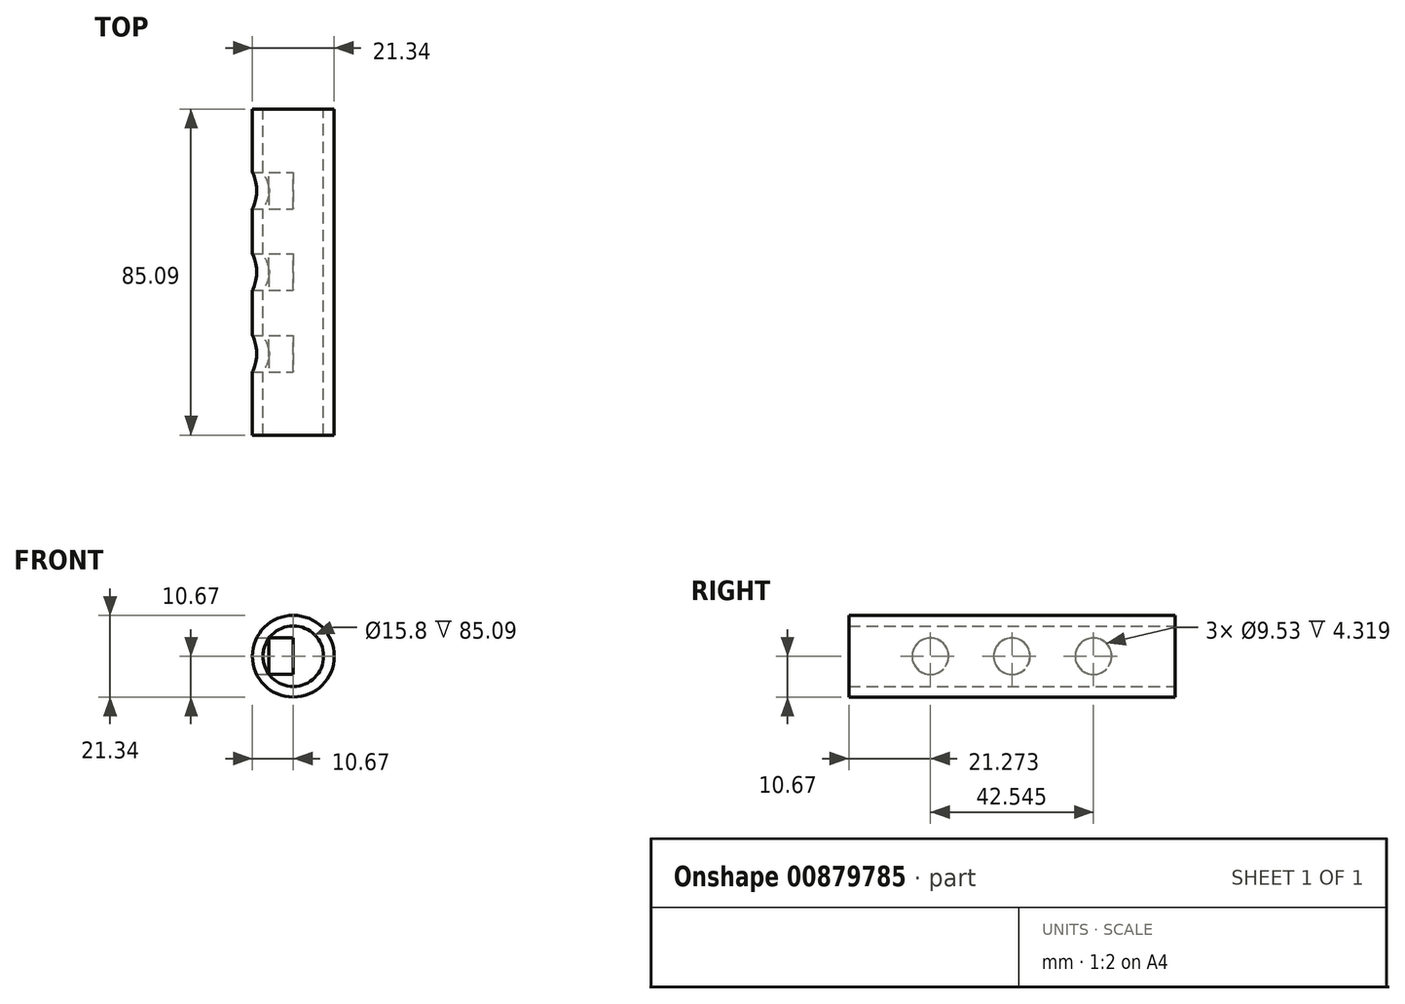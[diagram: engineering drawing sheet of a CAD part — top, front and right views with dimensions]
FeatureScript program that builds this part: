
annotation { "Feature Type Name" : "Feature", "Feature Type Description" : "" }
export const myFeature = defineFeature(function(context is Context, id is Id, definition is map)
    precondition{}
    {
        {
            var Q0;
            Q0=qCreatedBy(makeId("Front.planeOp"),FACE);
            var sketch = newSketch(context, id + "F0", { "sketchPlane" : qUnion([Q0])});
            skCircle(sketch, "E0", {"center": v(0, 0) * mm, "radius": 7.9 * mm});
            skCircle(sketch, "E1", {"center": v(0, 0) * mm, "radius": 10.67 * mm});
            skSolve(sketch);
        }
        {
            var Q0;
            Q0 = qSketchRegion(id + "F0", true);
            extrude(context, id + "F1", {"entities" : qUnion([Q0]), "depth" : 85.1 * mm, "offsetDistance" : 25.4 * mm});
        }
        {
            var Q0;
            Q0=qCreatedBy(makeId("Right.planeOp"),FACE);
            var sketch = newSketch(context, id + "F2", { "sketchPlane" : qUnion([Q0])});
            skCircle(sketch, "E2", {"center": v(-21.27, 0) * mm, "radius": 4.76 * mm});
            skCircle(sketch, "E3", {"center": v(-42.55, 0) * mm, "radius": 4.76 * mm});
            skCircle(sketch, "E4", {"center": v(-63.82, 0) * mm, "radius": 4.76 * mm});
            skSolve(sketch);
        }
        {
            var Q0;
            Q0 = qSketchRegion(id + "F2", true);
            extrude(context, id + "F3", {"entities" : qUnion([Q0]), "operationType" : NewBodyOperationType.REMOVE, "oppositeDirection" : true, "depth" : 25.4 * mm, "offsetDistance" : 25.4 * mm});
        }
        {
            var Q0;
            Q0=qCreatedBy(makeId("Right.planeOp"),FACE);
            var sketch = newSketch(context, id + "F4", { "sketchPlane" : qUnion([Q0])});
            skCircle(sketch, "E5", {"center": v(-21.27, 0) * mm, "radius": 4.76 * mm});
            skCircle(sketch, "E6", {"center": v(-42.55, 0) * mm, "radius": 4.76 * mm});
            skCircle(sketch, "E7", {"center": v(-63.82, 0) * mm, "radius": 4.76 * mm});
            skSolve(sketch);
        }
        {
            var Q0;
            Q0 = qSketchRegion(id + "F4", true);
            extrude(context, id + "F5", {"entities" : qUnion([Q0]), "operationType" : NewBodyOperationType.ADD, "oppositeDirection" : true, "depth" : 6.35 * mm, "offsetDistance" : 25.4 * mm});
        }
    });
